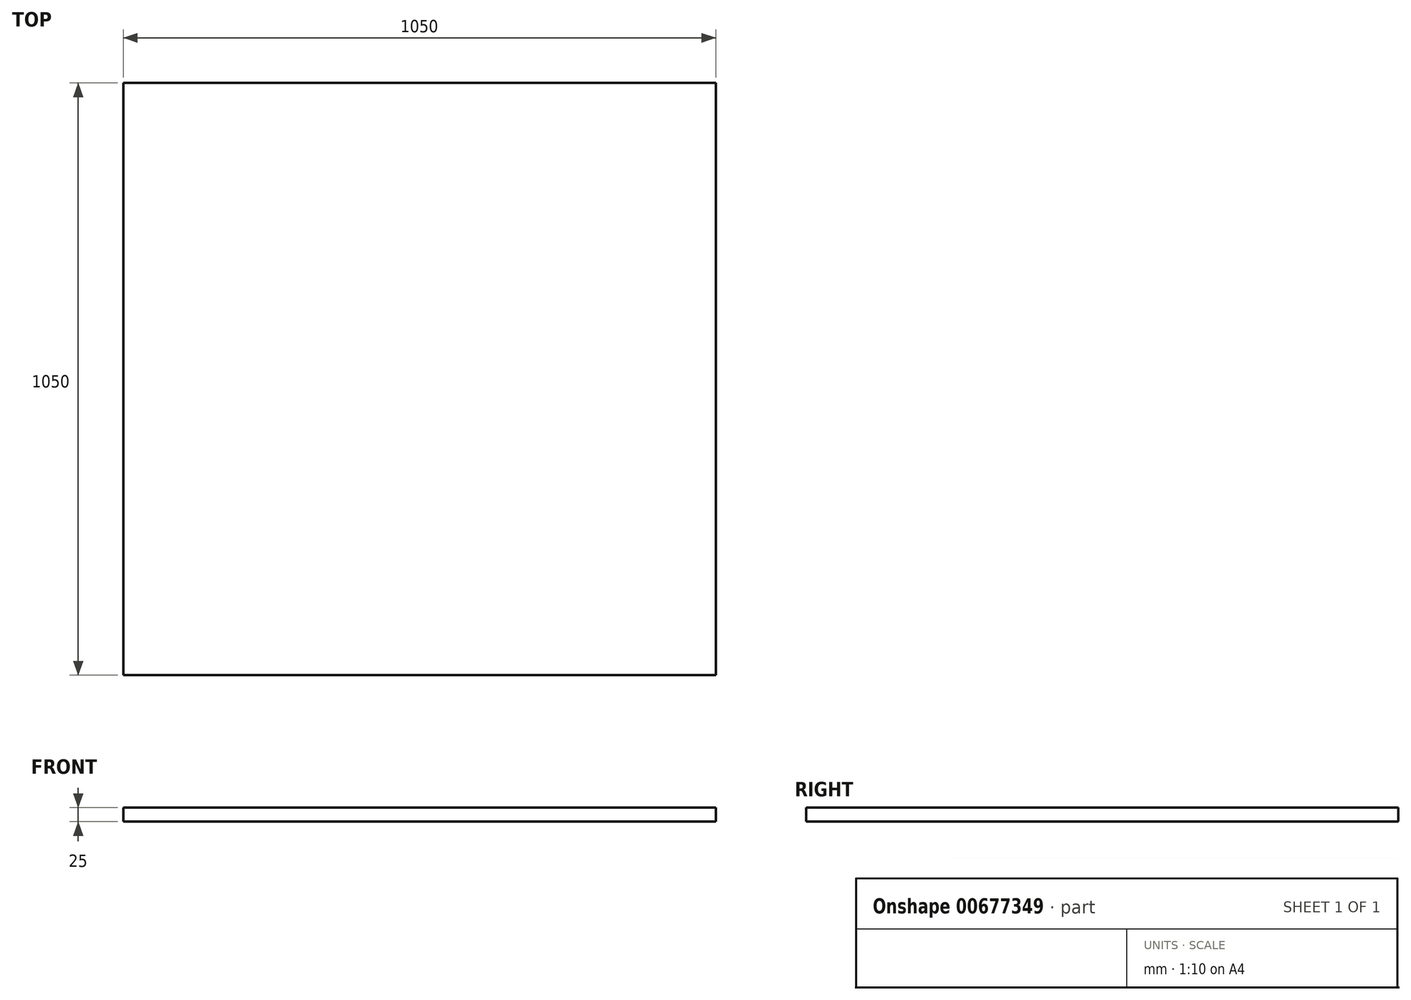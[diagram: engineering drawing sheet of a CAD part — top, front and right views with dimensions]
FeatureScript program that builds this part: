
annotation { "Feature Type Name" : "Feature", "Feature Type Description" : "" }
export const myFeature = defineFeature(function(context is Context, id is Id, definition is map)
    precondition{}
    {
        {
            var Q0;
            Q0=qCreatedBy(makeId("Top.planeOp"),FACE);
            var sketch = newSketch(context, id + "F0", { "sketchPlane" : qUnion([Q0])});
            skLineSegment(sketch, "E0.bottom", {"start": v(-525, 525) * mm, "end": v(525, 525) * mm});
            skLineSegment(sketch, "E0.top", {"start": v(-525, -525) * mm, "end": v(525, -525) * mm});
            skLineSegment(sketch, "E0.left", {"start": v(-525, 525) * mm, "end": v(-525, -525) * mm});
            skLineSegment(sketch, "E0.right", {"start": v(525, 525) * mm, "end": v(525, -525) * mm});
            skPoint(sketch, "E0.middle", {"position": v(0, 0) * mm});
            skSolve(sketch);
        }
        {
            var Q0;
            Q0=makeQuery(id+"F0.imprint","IMPRINT",FACE,{"disambiguationData":[TD([[makeQuery(id+"F0.imprint","IMPRINT",EDGE,{"derivedFrom":sQuery(id+"F0.wireOp",EDGE,"E0.bottom")}),-1.0]])]});
            extrude(context, id + "F1", {"entities" : qUnion([Q0]), "depth" : 25 * mm, "offsetDistance" : 25 * mm});
        }
    });
